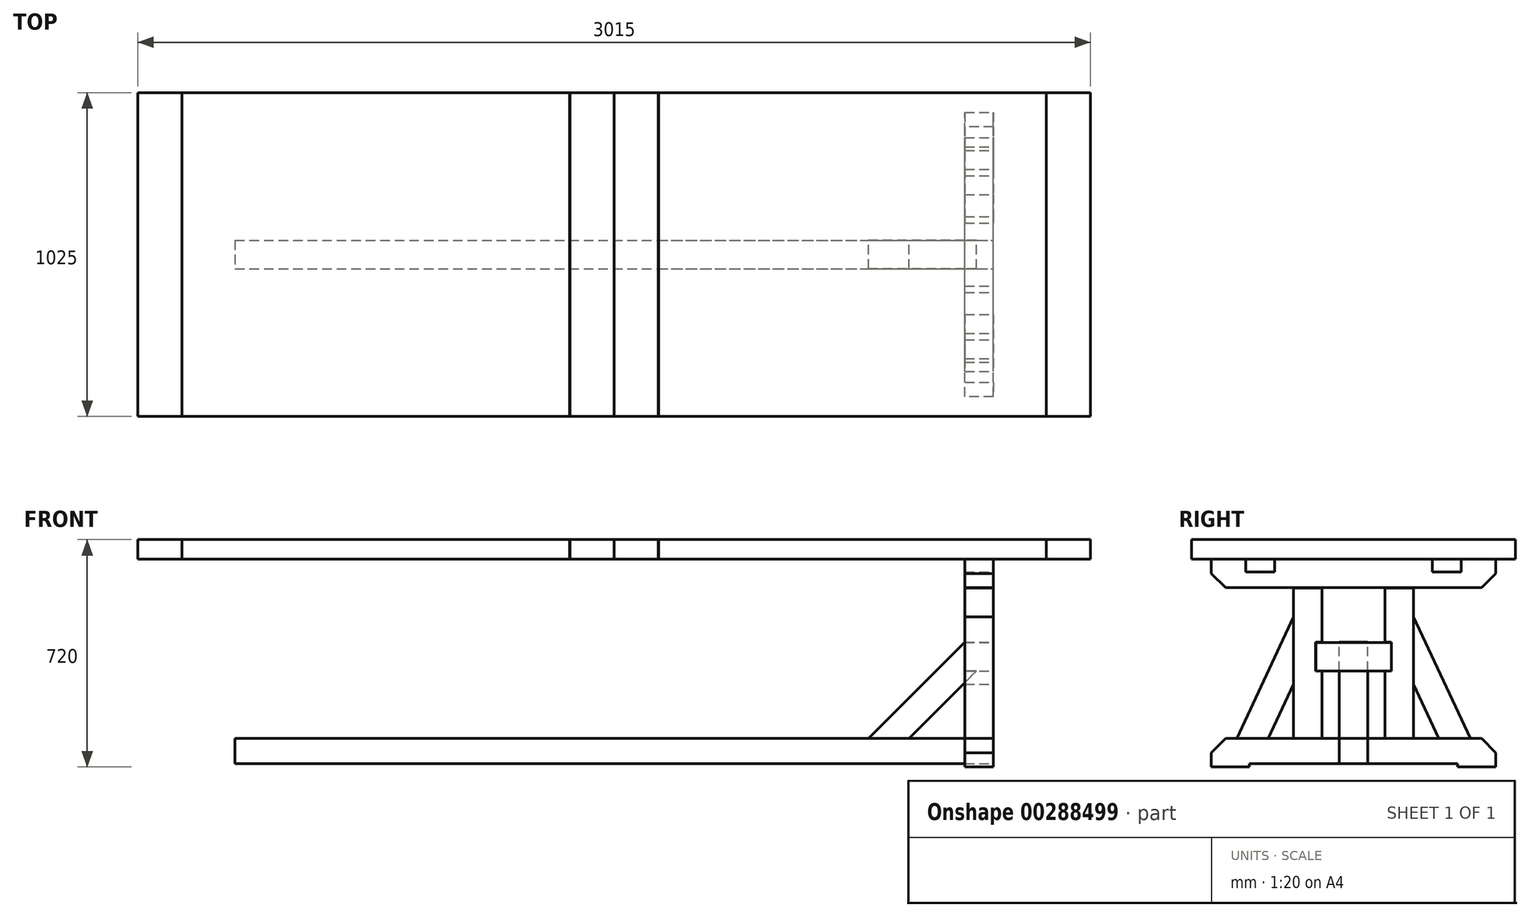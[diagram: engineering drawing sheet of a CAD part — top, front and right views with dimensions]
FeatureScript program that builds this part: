
annotation { "Feature Type Name" : "Feature", "Feature Type Description" : "" }
export const myFeature = defineFeature(function(context is Context, id is Id, definition is map)
    precondition{}
    {
        {
            var Q0;
            Q0=qCreatedBy(makeId("Top.planeOp"),FACE);
            var sketch = newSketch(context, id + "F0", { "sketchPlane" : qUnion([Q0])});
            skLineSegment(sketch, "E0.bottom", {"start": v(0, 512.5) * mm, "end": v(140, 512.5) * mm});
            skLineSegment(sketch, "E0.top", {"start": v(0, -512.5) * mm, "end": v(140, -512.5) * mm});
            skLineSegment(sketch, "E0.right", {"start": v(140, 512.5) * mm, "end": v(140, -512.5) * mm});
            skPoint(sketch, "E0.middle", {"position": v(0, 0) * mm});
            skLineSegment(sketch, "E1", {"start": v(0, 512.5) * mm, "end": v(0, -512.5) * mm});
            skPoint(sketch, "E2.orphan", {"position": v(-140, 512.5) * mm});
            skPoint(sketch, "E3.orphan", {"position": v(-140, -512.5) * mm});
            skSolve(sketch);
        }
        {
            var Q0;
            Q0=qCreatedBy(makeId("Top.planeOp"),FACE);
            cPlane(context, id + "F1", {"entities" : qUnion([Q0]), "cplaneType" : CPlaneType.OFFSET, "offset" : 720 * mm, "oppositeDirection" : true, "width" : 150 * mm, "height" : 150 * mm});
        }
        {
            var Q0;
            Q0=qCreatedBy(makeId("Right.planeOp"),FACE);
            cPlane(context, id + "F2", {"entities" : qUnion([Q0]), "cplaneType" : CPlaneType.OFFSET, "offset" : 1200 * mm, "width" : 150 * mm, "height" : 150 * mm});
        }
        {
            var Q0;
            Q0=qCreatedBy(makeId("Right.planeOp"),FACE);
            cPlane(context, id + "F3", {"entities" : qUnion([Q0]), "cplaneType" : CPlaneType.OFFSET, "offset" : 1200 * mm, "oppositeDirection" : true, "width" : 150 * mm, "height" : 150 * mm});
        }
        {
            var Q0;
            Q0 = qSketchRegion(id + "F0", true);
            extrude(context, id + "F4", {"entities" : qUnion([Q0]), "oppositeDirection" : true, "depth" : 62 * mm});
        }
        {
            var Q0;
            Q0=qCreatedBy(makeId("Top.planeOp"),FACE);
            var sketch = newSketch(context, id + "F5", { "sketchPlane" : qUnion([Q0])});
            skLineSegment(sketch, "E4.bottom", {"start": v(140.5, 512.5) * mm, "end": v(1367.5, 512.5) * mm});
            skLineSegment(sketch, "E4.top", {"start": v(140.5, -512.5) * mm, "end": v(1367.5, -512.5) * mm});
            skLineSegment(sketch, "E4.right", {"start": v(1367.5, 512.5) * mm, "end": v(1367.5, -512.5) * mm});
            skLineSegment(sketch, "E5", {"start": v(140.5, 512.5) * mm, "end": v(140.5, -512.5) * mm});
            skSolve(sketch);
        }
        {
            var Q0;
            Q0 = qSketchRegion(id + "F5", true);
            var Q1;
            Q1=makeQuery(id+"F4.opExtrude","CAP_FACE",FACE,{"disambiguationData":[OSD([sQuery(id+"F0.wireOp",EDGE,"E0.bottom"),sQuery(id+"F0.wireOp",EDGE,"E0.top"),sQuery(id+"F0.wireOp",EDGE,"E0.right"),sQuery(id+"F0.wireOp",EDGE,"E1")])],"isStart":false});
            extrude(context, id + "F6", {"entities" : qUnion([Q0]), "operationType" : NewBodyOperationType.ADD, "endBound" : BoundingType.UP_TO_SURFACE, "oppositeDirection" : true, "endBoundEntityFace" : qUnion([Q1]), "depth" : 25 * mm});
        }
        {
            var Q0;
            Q0=qCreatedBy(makeId("Top.planeOp"),FACE);
            var sketch = newSketch(context, id + "F7", { "sketchPlane" : qUnion([Q0])});
            skLineSegment(sketch, "E6.bottom", {"start": v(1368, 512.5) * mm, "end": v(1507.5, 512.5) * mm});
            skLineSegment(sketch, "E6.top", {"start": v(1368, -512.5) * mm, "end": v(1507.5, -512.5) * mm});
            skLineSegment(sketch, "E6.left", {"start": v(1368, 512.5) * mm, "end": v(1368, -512.5) * mm});
            skLineSegment(sketch, "E6.right", {"start": v(1507.5, 512.5) * mm, "end": v(1507.5, -512.5) * mm});
            skSolve(sketch);
        }
        {
            var Q0;
            Q0 = qSketchRegion(id + "F7", true);
            var Q1;
            Q1=makeQuery(id+"F6.opExtrude","CAP_FACE",FACE,{"disambiguationData":[OSD([sQuery(id+"F5.wireOp",EDGE,"E4.bottom"),sQuery(id+"F5.wireOp",EDGE,"E4.top"),sQuery(id+"F5.wireOp",EDGE,"E4.right"),sQuery(id+"F5.wireOp",EDGE,"E5")])],"isStart":false});
            extrude(context, id + "F8", {"entities" : qUnion([Q0]), "endBound" : BoundingType.UP_TO_SURFACE, "oppositeDirection" : true, "endBoundEntityFace" : qUnion([Q1]), "depth" : 25 * mm});
        }
        {
            var Q0;
            Q0=makeQuery(id+"F4.opExtrude","SWEPT_BODY",BODY,{"disambiguationData":[OSD([sQuery(id+"F0.wireOp",EDGE,"E0.bottom"),sQuery(id+"F0.wireOp",EDGE,"E0.top"),sQuery(id+"F0.wireOp",EDGE,"E0.right"),sQuery(id+"F0.wireOp",EDGE,"E1")])]});
            var Q1;
            Q1=qCreatedBy(makeId("Right.planeOp"),FACE);
            mirror(context, id + "F9", {"entities" : qUnion([Q0]), "mirrorPlane" : qUnion([Q1])});
        }
        {
            var Q0;
            Q0=makeQuery(id+"F6.opExtrude","SWEPT_BODY",BODY,{"disambiguationData":[OSD([sQuery(id+"F5.wireOp",EDGE,"E4.bottom"),sQuery(id+"F5.wireOp",EDGE,"E4.top"),sQuery(id+"F5.wireOp",EDGE,"E4.right"),sQuery(id+"F5.wireOp",EDGE,"E5")])]});
            var Q1;
            Q1=qCreatedBy(makeId("Right.planeOp"),FACE);
            mirror(context, id + "F10", {"entities" : qUnion([Q0]), "mirrorPlane" : qUnion([Q1])});
        }
        {
            var Q0;
            Q0=makeQuery(id+"F8.opExtrude","SWEPT_BODY",BODY,{"disambiguationData":[OSD([sQuery(id+"F7.wireOp",EDGE,"E6.bottom"),sQuery(id+"F7.wireOp",EDGE,"E6.top"),sQuery(id+"F7.wireOp",EDGE,"E6.left"),sQuery(id+"F7.wireOp",EDGE,"E6.right")])]});
            var Q1;
            Q1=qCreatedBy(makeId("Right.planeOp"),FACE);
            mirror(context, id + "F11", {"entities" : qUnion([Q0]), "mirrorPlane" : qUnion([Q1])});
        }
        {
            var Q0;
            Q0=qCreatedBy(id+"F2.planeOp",FACE);
            var sketch = newSketch(context, id + "F12", { "sketchPlane" : qUnion([Q0])});
            skLineSegment(sketch, "E7.top", {"start": v(-450, -152.5) * mm, "end": v(450, -152.5) * mm});
            skLineSegment(sketch, "E7.left", {"start": v(-450, -62.5) * mm, "end": v(-450, -152.5) * mm});
            skLineSegment(sketch, "E7.right", {"start": v(450, -62.5) * mm, "end": v(450, -152.5) * mm});
            skLineSegment(sketch, "E8", {"start": v(-450, -62.5) * mm, "end": v(450, -62.5) * mm});
            skSolve(sketch);
        }
        {
            var Q0;
            Q0=makeQuery(id+"F12.imprint","IMPRINT",FACE,{"disambiguationData":[TD([[makeQuery(id+"F12.imprint","IMPRINT",EDGE,{"derivedFrom":sQuery(id+"F12.wireOp",EDGE,"E7.top")}),1.0]])]});
            extrude(context, id + "F13", {"entities" : qUnion([Q0]), "oppositeDirection" : true, "depth" : 90 * mm});
        }
        {
            var Q0;
            Q0=makeQuery(id+"F13.opExtrude","SWEPT_EDGE",EDGE,{"disambiguationData":[OSD([sQuery(id+"F12.wireOp",EDGE,"E7.top"),sQuery(id+"F12.wireOp",EDGE,"E7.left")])]});
            var Q1;
            Q1=makeQuery(id+"F13.opExtrude","SWEPT_EDGE",EDGE,{"disambiguationData":[OSD([sQuery(id+"F12.wireOp",EDGE,"E7.top"),sQuery(id+"F12.wireOp",EDGE,"E7.right")])]});
            chamfer(context, id + "F14", {"entities" : qUnion([Q0, Q1]), "chamferType" : ChamferType.OFFSET_ANGLE, "width" : 45 * mm, "oppositeDirection" : false, "angle" : 45 * degree, "tangentPropagation" : true});
        }
        {
            var Q0;
            Q0=makeQuery(id+"F13.opExtrude","CAP_FACE",FACE,{"disambiguationData":[OSD([sQuery(id+"F12.wireOp",EDGE,"E7.top"),sQuery(id+"F12.wireOp",EDGE,"E7.left"),sQuery(id+"F12.wireOp",EDGE,"E7.right"),sQuery(id+"F12.wireOp",EDGE,"E8")])],"isStart":true});
            var sketch = newSketch(context, id + "F15", { "sketchPlane" : qUnion([Q0])});
            skLineSegment(sketch, "E9.bottom", {"start": v(-341, -62.5) * mm, "end": v(-250, -62.5) * mm});
            skLineSegment(sketch, "E9.top", {"start": v(-341, -102.5) * mm, "end": v(-250, -102.5) * mm});
            skLineSegment(sketch, "E9.left", {"start": v(-341, -62.5) * mm, "end": v(-341, -102.5) * mm});
            skLineSegment(sketch, "E9.right", {"start": v(-250, -62.5) * mm, "end": v(-250, -102.5) * mm});
            skLineSegment(sketch, "E10.MirrorCS", {"start": v(341, -62.5) * mm, "end": v(341, -102.5) * mm});
            skLineSegment(sketch, "E11.MirrorCS", {"start": v(250, -62.5) * mm, "end": v(250, -102.5) * mm});
            skLineSegment(sketch, "E12.MirrorCS", {"start": v(341, -62.5) * mm, "end": v(250, -62.5) * mm});
            skLineSegment(sketch, "E13.MirrorCS", {"start": v(341, -102.5) * mm, "end": v(250, -102.5) * mm});
            skSolve(sketch);
        }
        {
            var Q0;
            Q0=makeQuery(id+"F15.imprint","IMPRINT",FACE,{"disambiguationData":[TD([[makeQuery(id+"F15.imprint","IMPRINT",EDGE,{"derivedFrom":sQuery(id+"F15.wireOp",EDGE,"E9.bottom")}),-1.0]])]});
            var Q1;
            Q1=makeQuery(id+"F15.imprint","IMPRINT",FACE,{"disambiguationData":[TD([[makeQuery(id+"F15.imprint","IMPRINT",EDGE,{"derivedFrom":sQuery(id+"F15.wireOp",EDGE,"E10.MirrorCS")}),-1.0]])]});
            extrude(context, id + "F16", {"entities" : qUnion([Q0, Q1]), "operationType" : NewBodyOperationType.REMOVE, "endBound" : BoundingType.UP_TO_NEXT, "oppositeDirection" : true, "depth" : 25 * mm});
        }
        {
            var Q0;
            Q0=qCreatedBy(id+"F2.planeOp",FACE);
            var sketch = newSketch(context, id + "F17", { "sketchPlane" : qUnion([Q0])});
            skLineSegment(sketch, "E14", {"start": v(0, -630) * mm, "end": v(450, -630) * mm});
            skLineSegment(sketch, "E15", {"start": v(450, -630) * mm, "end": v(450, -720) * mm});
            skLineSegment(sketch, "E16", {"start": v(450, -720) * mm, "end": v(330, -720) * mm});
            skLineSegment(sketch, "E17", {"start": v(330, -720) * mm, "end": v(330, -710) * mm});
            skLineSegment(sketch, "E18", {"start": v(330, -710) * mm, "end": v(0, -710) * mm});
            skLineSegment(sketch, "E19.MirrorCS", {"start": v(-330, -720) * mm, "end": v(-330, -710) * mm});
            skLineSegment(sketch, "E20.MirrorCS", {"start": v(-450, -720) * mm, "end": v(-330, -720) * mm});
            skLineSegment(sketch, "E21.MirrorCS", {"start": v(-330, -710) * mm, "end": v(0, -710) * mm});
            skLineSegment(sketch, "E22.MirrorCS", {"start": v(-450, -630) * mm, "end": v(-450, -720) * mm});
            skLineSegment(sketch, "E23.MirrorCS", {"start": v(0, -630) * mm, "end": v(-450, -630) * mm});
            skSolve(sketch);
        }
        {
            var Q0;
            Q0=makeQuery(id+"F17.imprint","IMPRINT",FACE,{"disambiguationData":[TD([[makeQuery(id+"F17.imprint","IMPRINT",EDGE,{"derivedFrom":sQuery(id+"F17.wireOp",EDGE,"E14")}),-1.0]])]});
            extrude(context, id + "F18", {"entities" : qUnion([Q0]), "oppositeDirection" : true, "depth" : 90 * mm});
        }
        {
            var Q0;
            Q0=makeQuery(id+"F18.opExtrude","SWEPT_EDGE",EDGE,{"disambiguationData":[OSD([sQuery(id+"F17.wireOp",EDGE,"E22.MirrorCS"),sQuery(id+"F17.wireOp",EDGE,"E23.MirrorCS")])]});
            var Q1;
            Q1=makeQuery(id+"F18.opExtrude","SWEPT_EDGE",EDGE,{"disambiguationData":[OSD([sQuery(id+"F17.wireOp",EDGE,"E14"),sQuery(id+"F17.wireOp",EDGE,"E15")])]});
            chamfer(context, id + "F19", {"entities" : qUnion([Q0, Q1]), "chamferType" : ChamferType.OFFSET_ANGLE, "width" : 45 * mm, "oppositeDirection" : false, "angle" : 45 * degree, "tangentPropagation" : true});
        }
        {
            var Q0;
            Q0=qCreatedBy(id+"F2.planeOp",FACE);
            var sketch = newSketch(context, id + "F20", { "sketchPlane" : qUnion([Q0])});
            skLineSegment(sketch, "E24.bottom", {"start": v(-190, -153) * mm, "end": v(-100, -153) * mm});
            skLineSegment(sketch, "E24.top", {"start": v(-190, -629.5) * mm, "end": v(-100, -629.5) * mm});
            skLineSegment(sketch, "E24.left", {"start": v(-190, -153) * mm, "end": v(-190, -629.5) * mm});
            skLineSegment(sketch, "E24.right", {"start": v(-100, -153) * mm, "end": v(-100, -325.5) * mm});
            skLineSegment(sketch, "E25", {"start": v(-100, -325.5) * mm, "end": v(-120, -325.5) * mm});
            skLineSegment(sketch, "E26", {"start": v(-120, -325.5) * mm, "end": v(-120, -416.5) * mm});
            skLineSegment(sketch, "E27", {"start": v(-120, -416.5) * mm, "end": v(-100, -416.5) * mm});
            skLineSegment(sketch, "E28.trimOffspring", {"start": v(-100, -416.5) * mm, "end": v(-100, -629.5) * mm});
            skSolve(sketch);
        }
        {
            var Q0;
            Q0=makeQuery(id+"F20.imprint","IMPRINT",FACE,{"disambiguationData":[TD([[makeQuery(id+"F20.imprint","IMPRINT",EDGE,{"derivedFrom":sQuery(id+"F20.wireOp",EDGE,"E24.bottom")}),-1.0]])]});
            extrude(context, id + "F21", {"entities" : qUnion([Q0]), "oppositeDirection" : true, "depth" : 90 * mm});
        }
        {
            var Q0;
            Q0=makeQuery(id+"F21.opExtrude","SWEPT_BODY",BODY,{"disambiguationData":[OSD([sQuery(id+"F20.wireOp",EDGE,"E24.bottom"),sQuery(id+"F20.wireOp",EDGE,"E24.top"),sQuery(id+"F20.wireOp",EDGE,"E24.left"),sQuery(id+"F20.wireOp",EDGE,"E24.right")])]});
            var Q1;
            Q1=qCreatedBy(makeId("Front.planeOp"),FACE);
            mirror(context, id + "F22", {"entities" : qUnion([Q0]), "mirrorPlane" : qUnion([Q1])});
        }
        {
            var Q0;
            Q0=qCreatedBy(id+"F2.planeOp",FACE);
            var sketch = newSketch(context, id + "F23", { "sketchPlane" : qUnion([Q0])});
            skLineSegment(sketch, "E29.bottom", {"start": v(-119.5, -326) * mm, "end": v(119.5, -326) * mm});
            skLineSegment(sketch, "E29.top", {"start": v(-119.5, -416) * mm, "end": v(119.5, -416) * mm});
            skLineSegment(sketch, "E29.left", {"start": v(-119.5, -326) * mm, "end": v(-119.5, -416) * mm});
            skLineSegment(sketch, "E29.right", {"start": v(119.5, -326) * mm, "end": v(119.5, -416) * mm});
            skSolve(sketch);
        }
        {
            var Q0;
            Q0=makeQuery(id+"F23.imprint","IMPRINT",FACE,{"disambiguationData":[TD([[makeQuery(id+"F23.imprint","IMPRINT",EDGE,{"derivedFrom":sQuery(id+"F23.wireOp",EDGE,"E29.bottom")}),-1.0]])]});
            extrude(context, id + "F24", {"entities" : qUnion([Q0]), "oppositeDirection" : true, "depth" : 90 * mm});
        }
        {
            var Q0;
            Q0=qCreatedBy(id+"F2.planeOp",FACE);
            var sketch = newSketch(context, id + "F25", { "sketchPlane" : qUnion([Q0])});
            skLineSegment(sketch, "E30", {"start": v(-190, -244.82) * mm, "end": v(-369.61, -630) * mm});
            skLineSegment(sketch, "E31", {"start": v(-369.61, -630) * mm, "end": v(-270.3, -630) * mm});
            skLineSegment(sketch, "E32", {"start": v(-270.3, -630) * mm, "end": v(-190, -457.78) * mm});
            skLineSegment(sketch, "E33", {"start": v(-190, -457.78) * mm, "end": v(-190, -244.82) * mm});
            skSolve(sketch);
        }
        {
            var Q0;
            Q0=makeQuery(id+"F25.imprint","IMPRINT",FACE,{"disambiguationData":[TD([[makeQuery(id+"F25.imprint","IMPRINT",EDGE,{"derivedFrom":sQuery(id+"F25.wireOp",EDGE,"E30")}),1.0]])]});
            extrude(context, id + "F26", {"entities" : qUnion([Q0]), "oppositeDirection" : true, "depth" : 90 * mm});
        }
        {
            var Q0;
            Q0=makeQuery(id+"F26.opExtrude","SWEPT_BODY",BODY,{"disambiguationData":[OSD([sQuery(id+"F25.wireOp",EDGE,"E30"),sQuery(id+"F25.wireOp",EDGE,"E31"),sQuery(id+"F25.wireOp",EDGE,"E32"),sQuery(id+"F25.wireOp",EDGE,"E33")])]});
            var Q1;
            Q1=qCreatedBy(makeId("Front.planeOp"),FACE);
            mirror(context, id + "F27", {"entities" : qUnion([Q0]), "mirrorPlane" : qUnion([Q1])});
        }
        {
            var Q0;
            Q0=qCreatedBy(id+"F2.planeOp",FACE);
            var sketch = newSketch(context, id + "F28", { "sketchPlane" : qUnion([Q0])});
            skLineSegment(sketch, "E34.bottom", {"start": v(-45, -630) * mm, "end": v(45, -630) * mm});
            skLineSegment(sketch, "E34.top", {"start": v(-45, -710) * mm, "end": v(45, -710) * mm});
            skLineSegment(sketch, "E34.left", {"start": v(-45, -630) * mm, "end": v(-45, -710) * mm});
            skLineSegment(sketch, "E34.right", {"start": v(45, -630) * mm, "end": v(45, -710) * mm});
            skSolve(sketch);
        }
        {
            var Q0;
            Q0=makeQuery(id+"F28.imprint","IMPRINT",FACE,{"disambiguationData":[TD([[makeQuery(id+"F28.imprint","IMPRINT",EDGE,{"derivedFrom":sQuery(id+"F28.wireOp",EDGE,"E34.bottom")}),-1.0]])]});
            var Q1;
            Q1=qCreatedBy(id+"F3.planeOp",FACE);
            extrude(context, id + "F29", {"entities" : qUnion([Q0]), "endBound" : BoundingType.UP_TO_SURFACE, "oppositeDirection" : true, "endBoundEntityFace" : qUnion([Q1]), "depth" : 25 * mm});
        }
        {
            var Q0;
            Q0=qCreatedBy(makeId("Front.planeOp"),FACE);
            var sketch = newSketch(context, id + "F30", { "sketchPlane" : qUnion([Q0])});
            skLineSegment(sketch, "E35", {"start": v(1110, -325.5) * mm, "end": v(805.5, -630) * mm});
            skLineSegment(sketch, "E36", {"start": v(805.5, -630) * mm, "end": v(932.78, -630) * mm});
            skLineSegment(sketch, "E37", {"start": v(932.78, -630) * mm, "end": v(1146.28, -416.5) * mm});
            skLineSegment(sketch, "E38", {"start": v(1146.28, -416.5) * mm, "end": v(1110, -416.5) * mm});
            skLineSegment(sketch, "E39", {"start": v(1110, -416.5) * mm, "end": v(1110, -325.5) * mm});
            skSolve(sketch);
        }
        {
            var Q0;
            Q0=makeQuery(id+"F30.imprint","IMPRINT",FACE,{"disambiguationData":[TD([[makeQuery(id+"F30.imprint","IMPRINT",EDGE,{"derivedFrom":sQuery(id+"F30.wireOp",EDGE,"E35")}),1.0]])]});
            extrude(context, id + "F31", {"entities" : qUnion([Q0]), "endBound" : BoundingType.SYMMETRIC, "depth" : 90 * mm});
        }
    });
